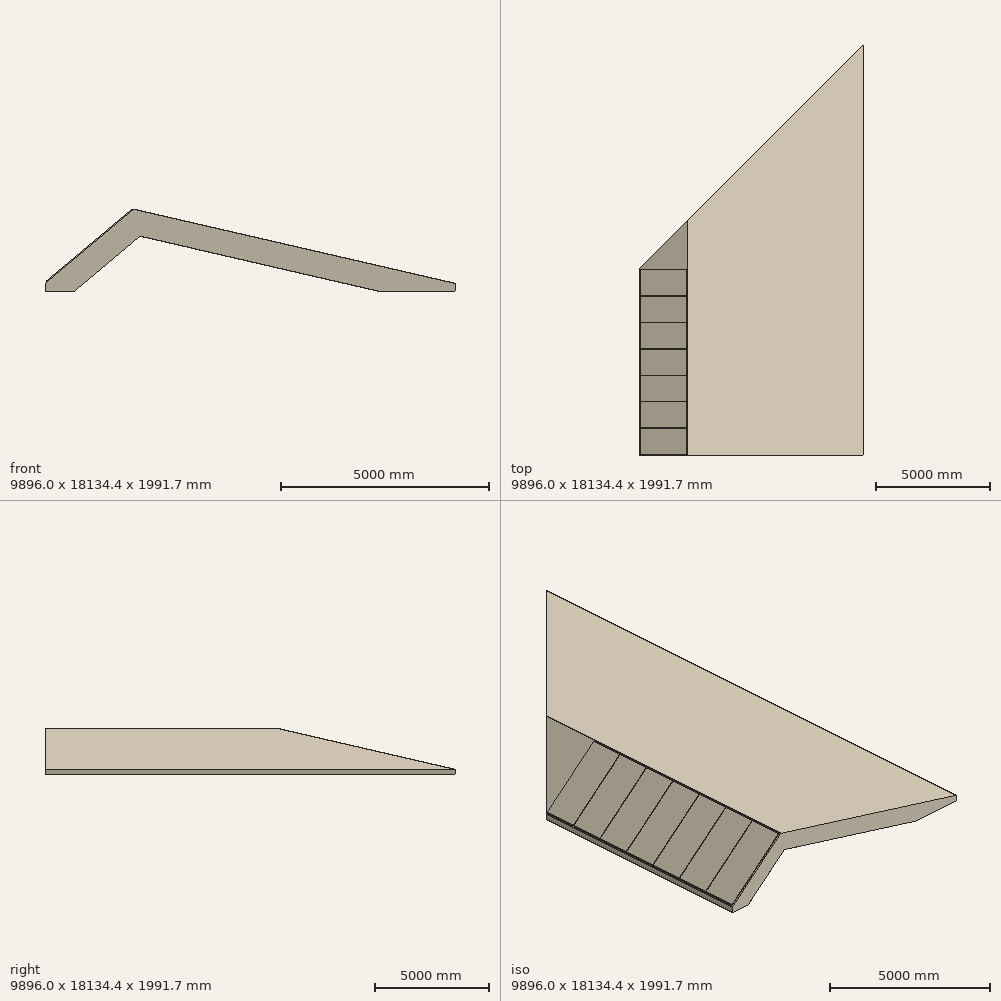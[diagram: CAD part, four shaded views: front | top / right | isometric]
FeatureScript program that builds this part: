
annotation { "Feature Type Name" : "Feature", "Feature Type Description" : "" }
export const myFeature = defineFeature(function(context is Context, id is Id, definition is map)
    precondition{}
    {
        {
            var Q0;
            Q0=qCreatedBy(makeId("Front.planeOp"),FACE);
            var sketch = newSketch(context, id + "F0", { "sketchPlane" : qUnion([Q0])});
            skLineSegment(sketch, "E0", {"start": v(0, 0) * mm, "end": v(2373.63, 1991.71) * mm});
            skLineSegment(sketch, "E1", {"start": v(2373.63, 1991.71) * mm, "end": v(11000.68, 0) * mm});
            skLineSegment(sketch, "E2", {"start": v(11000.68, 0) * mm, "end": v(0, 0) * mm});
            skLineSegment(sketch, "E3", {"start": v(8333.43, 0) * mm, "end": v(2530.14, 1339.8) * mm});
            skLineSegment(sketch, "E4", {"start": v(2530.14, 1339.8) * mm, "end": v(933.43, 0) * mm});
            skLineSegment(sketch, "E5", {"start": v(238.35, 200) * mm, "end": v(238.35, 0) * mm});
            skLineSegment(sketch, "E6", {"start": v(10134.39, 200) * mm, "end": v(10134.39, 0) * mm});
            skSolve(sketch);
        }
        {
            var Q0;
            {var subQ0=sQuery(id+"F0.wireOp",EDGE,"E3");Q0=makeQuery(id+"F0.imprint","IMPRINT",FACE,{"disambiguationData":[TD([[makeQuery(id+"F0.imprint","IMPRINT",EDGE,{"derivedFrom":subQ0}),-1.0]])]});}
            extrude(context, id + "F1", {"entities" : qUnion([Q0]), "depth" : 19000 * mm, "offsetDistance" : 25 * mm});
        }
        {
            var Q0;
            {var subQ0=sQuery(id+"F0.wireOp",EDGE,"E2");Q0=makeQuery(id+"F1.opExtrude","SWEPT_FACE",FACE,{"disambiguationData":[OSD([subQ0]),TDD([makeQuery(id+"F0.imprint","IMPRINT",EDGE,{"disambiguationData":[TD([[makeQuery(id+"F0.imprint","INTERSECT",VERTEX,{"derivedFrom":[subQ0,sQuery(id+"F0.wireOp",EDGE,"E4")]}),-1.0]])],"derivedFrom":subQ0})])]});}
            var sketch = newSketch(context, id + "F2", { "sketchPlane" : qUnion([Q0])});
            skLineSegment(sketch, "E7", {"start": v(0, 0) * mm, "end": v(11000, 11000) * mm});
            skLineSegment(sketch, "E8", {"start": v(11000, 11000) * mm, "end": v(11000, 0) * mm});
            skLineSegment(sketch, "E9", {"start": v(11000, 0) * mm, "end": v(0, 0) * mm});
            skLineSegment(sketch, "E10", {"start": v(11000, 11000) * mm, "end": v(0, 11000) * mm});
            skLineSegment(sketch, "E11", {"start": v(0, 11000) * mm, "end": v(0, 0) * mm});
            skLineSegment(sketch, "E12", {"start": v(0, 11000) * mm, "end": v(11000, 0) * mm});
            skSolve(sketch);
        }
        {
            var Q0;
            {var subQ0=sQuery(id+"F2.wireOp",EDGE,"E9");var subQ1=sQuery(id+"F2.wireOp",EDGE,"E7");var subQ2=makeQuery(id+"F2.imprint","INTERSECT",VERTEX,{"derivedFrom":[subQ1,subQ0,sQuery(id+"F2.wireOp",EDGE,"E11")]});Q0=makeQuery(id+"F2.imprint","IMPRINT",FACE,{"disambiguationData":[TD([[makeQuery(id+"F2.imprint","IMPRINT",EDGE,{"disambiguationData":[TD([[subQ2,-1.0]])],"derivedFrom":subQ1}),-1.0]])]});}
            var Q1;
            {var subQ0=sQuery(id+"F2.wireOp",EDGE,"E12");var subQ1=sQuery(id+"F2.wireOp",EDGE,"E10");var subQ2=makeQuery(id+"F2.imprint","INTERSECT",VERTEX,{"derivedFrom":[subQ1,sQuery(id+"F2.wireOp",EDGE,"E11"),subQ0]});Q1=makeQuery(id+"F2.imprint","IMPRINT",FACE,{"disambiguationData":[TD([[makeQuery(id+"F2.imprint","IMPRINT",EDGE,{"disambiguationData":[TD([[subQ2,1.0]])],"derivedFrom":subQ1}),1.0]])]});}
            var Q2;
            {var subQ0=sQuery(id+"F2.wireOp",EDGE,"E11");Q2=makeQuery(id+"F2.imprint","IMPRINT",FACE,{"disambiguationData":[TD([[makeQuery(id+"F2.imprint","IMPRINT",EDGE,{"derivedFrom":subQ0}),1.0]])]});}
            var Q3;
            {var subQ0=sQuery(id+"F2.wireOp",EDGE,"E12");var subQ1=sQuery(id+"F2.wireOp",EDGE,"E7");var subQ2=makeQuery(id+"F2.imprint","INTERSECT",VERTEX,{"derivedFrom":[subQ1,subQ0]});Q3=makeQuery(id+"F2.imprint","IMPRINT",FACE,{"disambiguationData":[TD([[makeQuery(id+"F2.imprint","IMPRINT",EDGE,{"disambiguationData":[TD([[subQ2,1.0]])],"derivedFrom":subQ1}),-1.0]])]});}
            var Q4;
            {var subQ0=sQuery(id+"F2.wireOp",EDGE,"E7");var subQ1=sQuery(id+"F0.wireOp",EDGE,"E2");var subQ2=makeQuery(id+"F1.opExtrude","SWEPT_EDGE",EDGE,{"disambiguationData":[OSD([subQ1,sQuery(id+"F0.wireOp",EDGE,"E5")])]});var subQ3=makeQuery(id+"F2.imprint","INTERSECT",VERTEX,{"derivedFrom":[subQ2,subQ0]});Q4=makeQuery(id+"F2.imprint","IMPRINT",FACE,{"disambiguationData":[TD([[makeQuery(id+"F2.imprint","IMPRINT",EDGE,{"disambiguationData":[TD([[subQ3,-1.0]])],"derivedFrom":subQ0}),-1.0]])]});}
            var Q5;
            {var subQ0=sQuery(id+"F2.wireOp",EDGE,"E7");var subQ1=sQuery(id+"F0.wireOp",EDGE,"E2");var subQ2=makeQuery(id+"F1.opExtrude","SWEPT_EDGE",EDGE,{"disambiguationData":[OSD([subQ1,sQuery(id+"F0.wireOp",EDGE,"E5")])]});var subQ3=makeQuery(id+"F2.imprint","INTERSECT",VERTEX,{"derivedFrom":[subQ2,subQ0]});Q5=makeQuery(id+"F2.imprint","IMPRINT",FACE,{"disambiguationData":[TD([[makeQuery(id+"F2.imprint","IMPRINT",EDGE,{"disambiguationData":[TD([[subQ3,-1.0]])],"derivedFrom":subQ0}),1.0]])]});}
            var Q6;
            {var subQ0=sQuery(id+"F2.wireOp",EDGE,"E12");var subQ1=sQuery(id+"F2.wireOp",EDGE,"E7");var subQ2=makeQuery(id+"F2.imprint","INTERSECT",VERTEX,{"derivedFrom":[subQ1,subQ0]});Q6=makeQuery(id+"F2.imprint","IMPRINT",FACE,{"disambiguationData":[TD([[makeQuery(id+"F2.imprint","IMPRINT",EDGE,{"disambiguationData":[TD([[subQ2,1.0]])],"derivedFrom":subQ1}),1.0]])]});}
            extrude(context, id + "F3", {"entities" : qUnion([Q0, Q1, Q2, Q3, Q4, Q5, Q6]), "operationType" : NewBodyOperationType.REMOVE, "endBound" : BoundingType.THROUGH_ALL, "oppositeDirection" : true, "depth" : 25 * mm, "offsetDistance" : 25 * mm});
        }
        {
            var Q0;
            Q0=makeQuery(id+"F1.opExtrude","SWEPT_FACE",FACE,{"disambiguationData":[OSD([sQuery(id+"F0.wireOp",EDGE,"E0")])]});
            var sketch = newSketch(context, id + "F4", { "sketchPlane" : qUnion([Q0])});
            skLineSegment(sketch, "E13.bottom", {"start": v(3061.14, -18950) * mm, "end": v(361.14, -18950) * mm});
            skLineSegment(sketch, "E13.top", {"start": v(3061.14, -17800) * mm, "end": v(361.14, -17800) * mm});
            skLineSegment(sketch, "E13.left", {"start": v(3061.14, -18950) * mm, "end": v(3061.14, -17800) * mm});
            skLineSegment(sketch, "E13.right", {"start": v(361.14, -18950) * mm, "end": v(361.14, -17800) * mm});
            skLineSegment(sketch, "E14.0.1.0", {"start": v(3061.14, -17780) * mm, "end": v(361.14, -17780) * mm});
            skLineSegment(sketch, "E14.0.1.1", {"start": v(3061.14, -16630) * mm, "end": v(361.14, -16630) * mm});
            skLineSegment(sketch, "E14.0.1.2", {"start": v(361.14, -17780) * mm, "end": v(361.14, -16630) * mm});
            skLineSegment(sketch, "E14.0.1.3", {"start": v(3061.14, -17780) * mm, "end": v(3061.14, -16630) * mm});
            skLineSegment(sketch, "E14.0.2.0", {"start": v(3061.14, -16610) * mm, "end": v(361.14, -16610) * mm});
            skLineSegment(sketch, "E14.0.2.1", {"start": v(3061.14, -15460) * mm, "end": v(361.14, -15460) * mm});
            skLineSegment(sketch, "E14.0.2.2", {"start": v(361.14, -16610) * mm, "end": v(361.14, -15460) * mm});
            skLineSegment(sketch, "E14.0.2.3", {"start": v(3061.14, -16610) * mm, "end": v(3061.14, -15460) * mm});
            skLineSegment(sketch, "E14.0.3.0", {"start": v(3061.14, -15440) * mm, "end": v(361.14, -15440) * mm});
            skLineSegment(sketch, "E14.0.3.1", {"start": v(3061.14, -14290) * mm, "end": v(361.14, -14290) * mm});
            skLineSegment(sketch, "E14.0.3.2", {"start": v(361.14, -15440) * mm, "end": v(361.14, -14290) * mm});
            skLineSegment(sketch, "E14.0.3.3", {"start": v(3061.14, -15440) * mm, "end": v(3061.14, -14290) * mm});
            skLineSegment(sketch, "E14.0.4.0", {"start": v(3061.14, -14270) * mm, "end": v(361.14, -14270) * mm});
            skLineSegment(sketch, "E14.0.4.1", {"start": v(3061.14, -13120) * mm, "end": v(361.14, -13120) * mm});
            skLineSegment(sketch, "E14.0.4.2", {"start": v(361.14, -14270) * mm, "end": v(361.14, -13120) * mm});
            skLineSegment(sketch, "E14.0.4.3", {"start": v(3061.14, -14270) * mm, "end": v(3061.14, -13120) * mm});
            skLineSegment(sketch, "E14.0.5.0", {"start": v(3061.14, -13100) * mm, "end": v(361.14, -13100) * mm});
            skLineSegment(sketch, "E14.0.5.1", {"start": v(3061.14, -11950) * mm, "end": v(361.14, -11950) * mm});
            skLineSegment(sketch, "E14.0.5.2", {"start": v(361.14, -13100) * mm, "end": v(361.14, -11950) * mm});
            skLineSegment(sketch, "E14.0.5.3", {"start": v(3061.14, -13100) * mm, "end": v(3061.14, -11950) * mm});
            skLineSegment(sketch, "E14.direction1", {"start": v(361.14, -18950) * mm, "end": v(3061.14, -18950) * mm, "construction": true});
            skLineSegment(sketch, "E14.direction2", {"start": v(361.14, -18950) * mm, "end": v(361.14, -17780) * mm, "construction": true});
            skLineSegment(sketch, "E15.0.0.6", {"start": v(3061.14, -11930) * mm, "end": v(361.14, -11930) * mm});
            skLineSegment(sketch, "E15.3.0.6", {"start": v(3061.14, -10780) * mm, "end": v(361.14, -10780) * mm});
            skLineSegment(sketch, "E15.6.0.6", {"start": v(361.14, -11930) * mm, "end": v(361.14, -10780) * mm});
            skLineSegment(sketch, "E15.9.0.6", {"start": v(3061.14, -11930) * mm, "end": v(3061.14, -10780) * mm});
            skSolve(sketch);
        }
        {
            var Q0;
            Q0=makeQuery(id+"F4.imprint","IMPRINT",FACE,{"disambiguationData":[TD([[makeQuery(id+"F4.imprint","IMPRINT",EDGE,{"derivedFrom":sQuery(id+"F4.wireOp",EDGE,"E13.bottom")}),-1.0]])]});
            var Q1;
            Q1=makeQuery(id+"F4.imprint","IMPRINT",FACE,{"disambiguationData":[TD([[makeQuery(id+"F4.imprint","IMPRINT",EDGE,{"derivedFrom":sQuery(id+"F4.wireOp",EDGE,"E14.0.1.0")}),-1.0]])]});
            var Q2;
            Q2=makeQuery(id+"F4.imprint","IMPRINT",FACE,{"disambiguationData":[TD([[makeQuery(id+"F4.imprint","IMPRINT",EDGE,{"derivedFrom":sQuery(id+"F4.wireOp",EDGE,"E14.0.2.0")}),-1.0]])]});
            var Q3;
            Q3=makeQuery(id+"F4.imprint","IMPRINT",FACE,{"disambiguationData":[TD([[makeQuery(id+"F4.imprint","IMPRINT",EDGE,{"derivedFrom":sQuery(id+"F4.wireOp",EDGE,"E14.0.3.0")}),-1.0]])]});
            var Q4;
            Q4=makeQuery(id+"F4.imprint","IMPRINT",FACE,{"disambiguationData":[TD([[makeQuery(id+"F4.imprint","IMPRINT",EDGE,{"derivedFrom":sQuery(id+"F4.wireOp",EDGE,"E14.0.4.0")}),-1.0]])]});
            var Q5;
            Q5=makeQuery(id+"F4.imprint","IMPRINT",FACE,{"disambiguationData":[TD([[makeQuery(id+"F4.imprint","IMPRINT",EDGE,{"derivedFrom":sQuery(id+"F4.wireOp",EDGE,"E14.1.0.0")}),-1.0]])]});
            var Q6;
            Q6=makeQuery(id+"F4.imprint","IMPRINT",FACE,{"disambiguationData":[TD([[makeQuery(id+"F4.imprint","IMPRINT",EDGE,{"derivedFrom":sQuery(id+"F4.wireOp",EDGE,"E14.1.1.0")}),-1.0]])]});
            var Q7;
            Q7=makeQuery(id+"F4.imprint","IMPRINT",FACE,{"disambiguationData":[TD([[makeQuery(id+"F4.imprint","IMPRINT",EDGE,{"derivedFrom":sQuery(id+"F4.wireOp",EDGE,"E14.1.2.0")}),-1.0]])]});
            var Q8;
            Q8=makeQuery(id+"F4.imprint","IMPRINT",FACE,{"disambiguationData":[TD([[makeQuery(id+"F4.imprint","IMPRINT",EDGE,{"derivedFrom":sQuery(id+"F4.wireOp",EDGE,"E14.1.3.0")}),-1.0]])]});
            var Q9;
            Q9=makeQuery(id+"F4.imprint","IMPRINT",FACE,{"disambiguationData":[TD([[makeQuery(id+"F4.imprint","IMPRINT",EDGE,{"derivedFrom":sQuery(id+"F4.wireOp",EDGE,"E14.1.4.0")}),-1.0]])]});
            var Q10;
            Q10=makeQuery(id+"F4.imprint","IMPRINT",FACE,{"disambiguationData":[TD([[makeQuery(id+"F4.imprint","IMPRINT",EDGE,{"derivedFrom":sQuery(id+"F4.wireOp",EDGE,"E14.1.5.0")}),-1.0]])]});
            var Q11;
            Q11=makeQuery(id+"F4.imprint","IMPRINT",FACE,{"disambiguationData":[TD([[makeQuery(id+"F4.imprint","IMPRINT",EDGE,{"derivedFrom":sQuery(id+"F4.wireOp",EDGE,"E14.0.5.0")}),-1.0]])]});
            var Q12;
            Q12=makeQuery(id+"F4.imprint","IMPRINT",FACE,{"disambiguationData":[TD([[makeQuery(id+"F4.imprint","IMPRINT",EDGE,{"derivedFrom":sQuery(id+"F4.wireOp",EDGE,"E15.0.0.6")}),-1.0]])]});
            extrude(context, id + "F5", {"entities" : qUnion([Q0, Q1, Q2, Q3, Q4, Q5, Q6, Q7, Q8, Q9, Q10, Q11, Q12]), "operationType" : NewBodyOperationType.ADD, "depth" : 25 * mm, "offsetDistance" : 25 * mm});
        }
    });
